# Revit family: Accessory-Tissue_Holder-KOHLER-Coralais-K-13434
name_source: partatom
category: Generic Models
revit_build: Autodesk Revit 2015 (Build: 20140606_1530(x64)
units: mm (PartAtom-declared; Revit-internal decimal feet)

## types (3) — shared parameters
ADA Compliant = Yes
Assembly Code = C1030200
Date Modified = 09/11/2017
Default Elevation = 42"
Description = Coralais Toilet Tissue Holder
Height = 3 5/8"
Inlet Connector = Inlet Connection
Length = 8 1/2"
Manufacturer = Kohler
MasterFormat 1995 = 10820
MasterFormat 2004 = 10.28.13
Material = Premium Metal
Outlet Connector = Outlet Connection
Product Documentation Link = http://www.us.kohler.com
Product Name = Coralais
Product Page URL = http://www.us.kohler.com
URL = http://www.us.kohler.com
Width = 2 1/4"

## per-type parameters (varying)
| type | Finish | Model | Type |
| CP-Polished Chrome | Kohler-Metal-CP-Polished_Chrome | K-13434-CP | 1 |
| G-Brushed Chrome | Kohler-Metal-G-Brushed_Chrome | K-13434-G | 2 |
| BN-Vibrant Brushed Nickel | Kohler-Metal-BN-Vibrant_Brushed_Nickel | K-13434-BN | 3 |

## geometry (parser evidence)
native form markers: Sweep x6
no freeform markers — native parametric forms only
